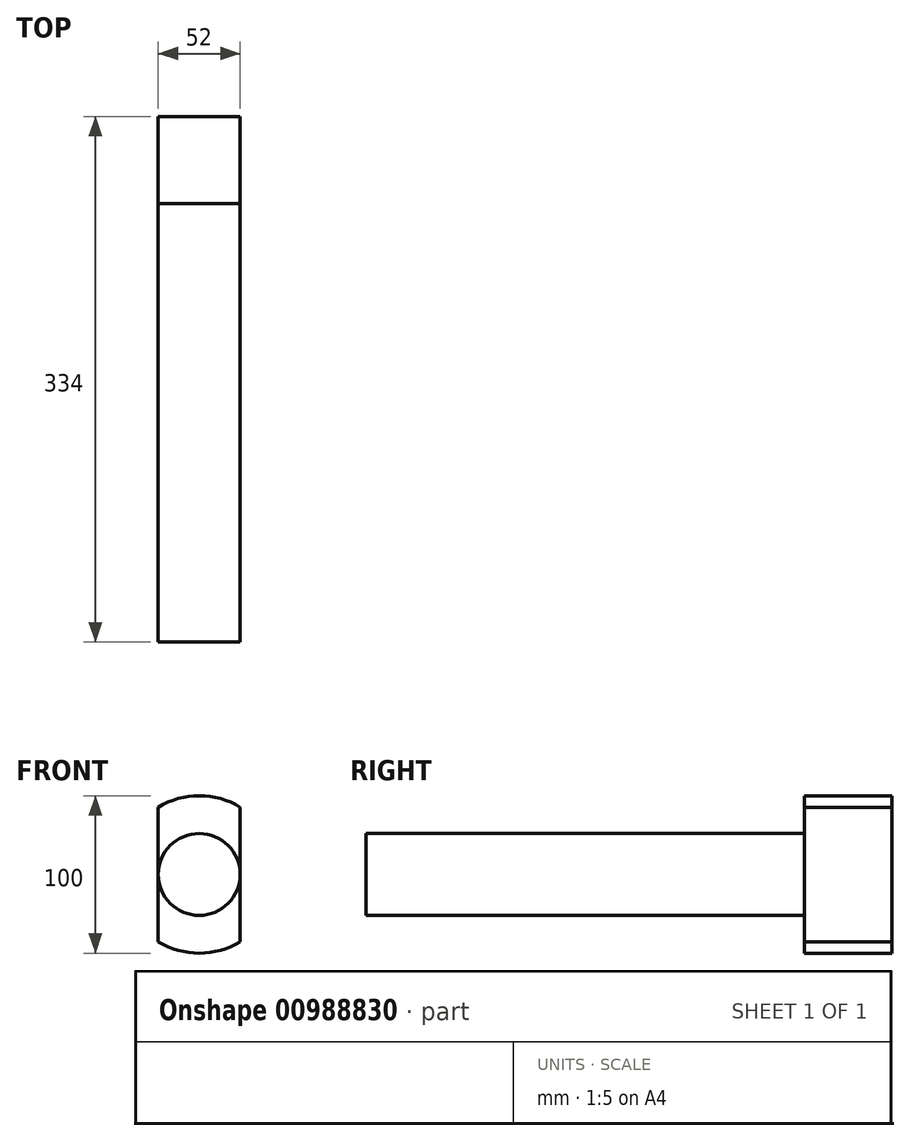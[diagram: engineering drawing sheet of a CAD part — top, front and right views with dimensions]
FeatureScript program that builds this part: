
annotation { "Feature Type Name" : "Feature", "Feature Type Description" : "" }
export const myFeature = defineFeature(function(context is Context, id is Id, definition is map)
    precondition{}
    {
        {
            var Q0;
            Q0=qCreatedBy(makeId("Front.planeOp"),FACE);
            var sketch = newSketch(context, id + "F0", { "sketchPlane" : qUnion([Q0])});
            skLineSegment(sketch, "E0.bottom", {"start": v(26, -26) * mm, "end": v(-26, -26) * mm});
            skLineSegment(sketch, "E0.top", {"start": v(26, 26) * mm, "end": v(-26, 26) * mm});
            skLineSegment(sketch, "E0.left", {"start": v(26, -26) * mm, "end": v(26, 26) * mm});
            skLineSegment(sketch, "E0.right", {"start": v(-26, -26) * mm, "end": v(-26, 26) * mm});
            skPoint(sketch, "E0.middle", {"position": v(0, 0) * mm});
            skCircle(sketch, "E1", {"center": v(0, 0) * mm, "radius": 26 * mm});
            skArc(sketch, "E2", {"start": v(-26, -42.7) * mm, "mid": v(0, -50) * mm, "end": v(26, -42.7) * mm});
            skLineSegment(sketch, "E3", {"start": v(-26, 26) * mm, "end": v(-26, 42.7) * mm});
            skLineSegment(sketch, "E4", {"start": v(26, 26) * mm, "end": v(26, 42.7) * mm});
            skLineSegment(sketch, "E5", {"start": v(-26, -26) * mm, "end": v(-26, -42.7) * mm});
            skLineSegment(sketch, "E6", {"start": v(26, -26) * mm, "end": v(26, -42.7) * mm});
            skArc(sketch, "E7.trimOffspring", {"start": v(26, 42.7) * mm, "mid": v(0, 50) * mm, "end": v(-26, 42.7) * mm});
            skSolve(sketch);
        }
        {
            var Q0;
            {var subQ0=sQuery(id+"F0.wireOp",EDGE,"E1");var subQ1=makeQuery(id+"F0.imprint","INTERSECT",VERTEX,{"derivedFrom":[sQuery(id+"F0.wireOp",EDGE,"E0.top"),subQ0]});Q0=makeQuery(id+"F0.imprint","IMPRINT",FACE,{"disambiguationData":[TD([[makeQuery(id+"F0.imprint","IMPRINT",EDGE,{"disambiguationData":[TD([[subQ1,1.0]])],"derivedFrom":subQ0}),1.0]])]});}
            extrude(context, id + "F1", {"entities" : qUnion([Q0]), "depth" : 278.5 * mm, "offsetDistance" : 25 * mm});
        }
        {
            var Q0;
            Q0 = qSketchRegion(id + "F0", true);
            extrude(context, id + "F2", {"entities" : qUnion([Q0]), "operationType" : NewBodyOperationType.ADD, "oppositeDirection" : true, "depth" : 55.5 * mm, "offsetDistance" : 25 * mm});
        }
    });
